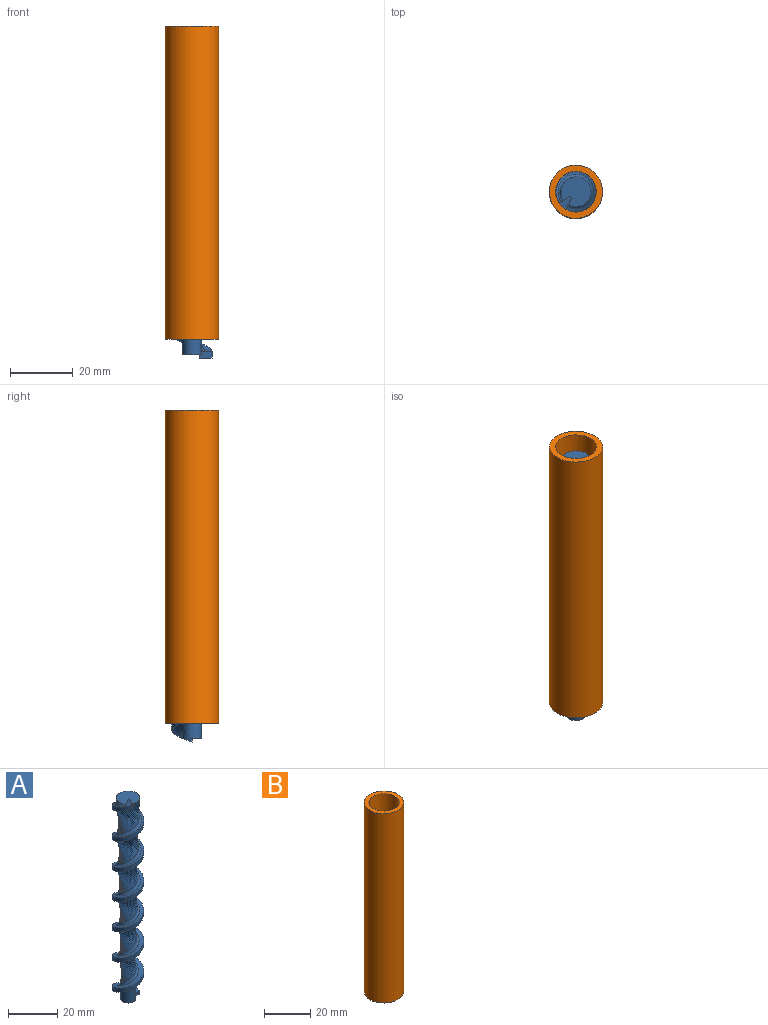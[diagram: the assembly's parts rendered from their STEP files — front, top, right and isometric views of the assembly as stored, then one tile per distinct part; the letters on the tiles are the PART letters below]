
ASSEMBLY  parts=2 mates=1
PART A: 12 faces, bbox 13.3x13.3x104.1 mm
  f0: plane 4.32x3.49mm, normal (0,-1,0), area 7.6mm2, adj f2,f3,f4,f6,f8,f9,f10
  f1: plane 3.68x3.29mm, normal (0.87,-0.5,0), area 5.9mm2, adj f3,f4,f5,f6,f7,f8,f11
  f2: cylinder r=2.4mm len=1mm, axis (0,0,1), area 0.5mm2, adj f0,f4,f9
  f3: bspline ~101.25x12.8mm, area 390.1mm2, adj f0,f1,f5,f6,f7,f10
  f4: bspline ~101.25x12.8mm, area 402.4mm2, adj f0,f1,f2,f6,f9,f11
  f5: cylinder r=2.4mm len=1mm, axis (0,0,1), area 0.5mm2, adj f1,f3,f7
  f6: cylinder r=6.4mm len=102mm, axis (0,0,1), area 535.3mm2, adj f0,f1,f3,f4
  f7: plane 10.03x10.03mm, normal (0,0,1), area 67.7mm2, adj f1,f3,f5,f8,f10
  f8: cone r=3mm half-angle=1deg, axis (0,0,1), area 1766.5mm2, adj f0,f1,f7,f9,f10,f11
  f9: plane 7.07x6.46mm, normal (0,0,-1), area 27.9mm2, adj f0,f2,f4,f8,f11
  f10: bspline ~100.62x11.32mm, area 309.8mm2, adj f0,f3,f7,f8
  f11: bspline ~100.78x11.19mm, area 301.6mm2, adj f1,f4,f8,f9
PART B: 4 faces, bbox 17x17x100 mm
  f0: cylinder r=6.5mm len=100mm, axis (0,0,-1), area 4084.1mm2, adj f2,f3
  f1: cylinder r=8.5mm len=100mm, axis (0,0,-1), area 5340.7mm2, adj f2,f3
  f2: plane 17x17mm, normal (0,0,1), area 94.2mm2, adj f0,f1
  f3: plane 17x17mm, normal (0,0,-1), area 94.2mm2, adj f0,f1
PLACE A t=(-49.21,11.57,11.02)mm
PLACE B t=(-49.21,11.57,16.02)mm
MATE fastened A.f2 <-> B.f1  axis (0,0,1) through (-49.21,11.57,61.02)mm
